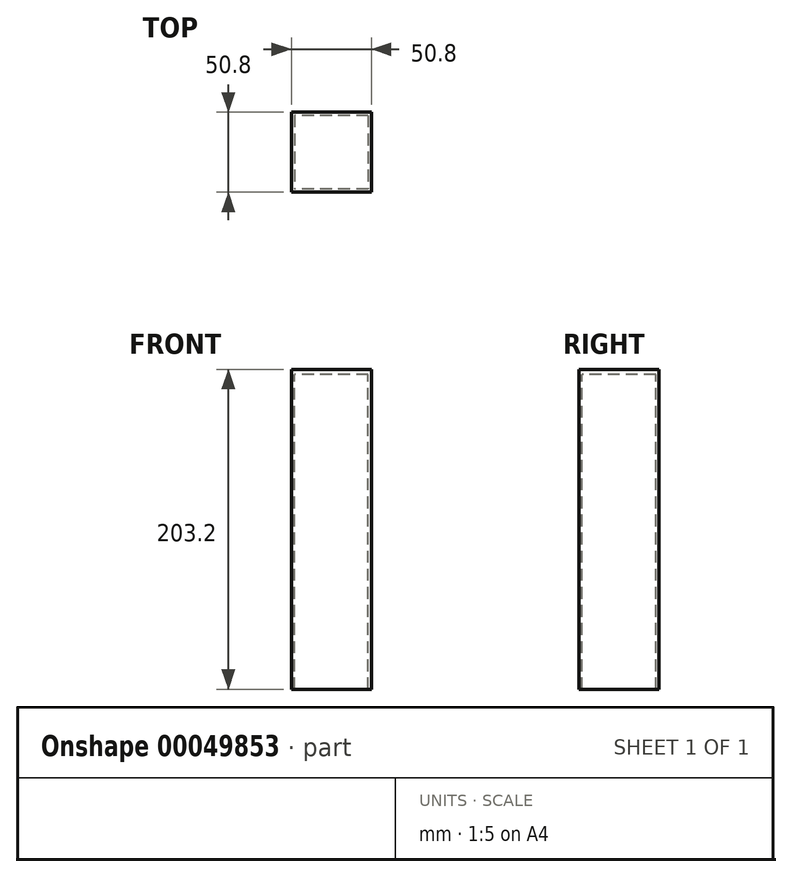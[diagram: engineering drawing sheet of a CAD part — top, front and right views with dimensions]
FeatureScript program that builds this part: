
annotation { "Feature Type Name" : "Feature", "Feature Type Description" : "" }
export const myFeature = defineFeature(function(context is Context, id is Id, definition is map)
    precondition{}
    {
        {
            var Q0;
            Q0=qCreatedBy(makeId("Top.planeOp"),FACE);
            var sketch = newSketch(context, id + "F0", { "sketchPlane" : qUnion([Q0])});
            skLineSegment(sketch, "E0.rect.bottom", {"start": v(25.4, 25.4) * mm, "end": v(-25.4, 25.4) * mm});
            skLineSegment(sketch, "E0.rect.top", {"start": v(25.4, -25.4) * mm, "end": v(-25.4, -25.4) * mm});
            skLineSegment(sketch, "E0.rect.left", {"start": v(25.4, 25.4) * mm, "end": v(25.4, -25.4) * mm});
            skLineSegment(sketch, "E0.rect.right", {"start": v(-25.4, 25.4) * mm, "end": v(-25.4, -25.4) * mm});
            skPoint(sketch, "E0.rect.middle", {"position": v(0, 0) * mm});
            skLineSegment(sketch, "E1.0", {"start": v(23.4, 23.4) * mm, "end": v(-23.4, 23.4) * mm});
            skLineSegment(sketch, "E1.1", {"start": v(23.4, 23.4) * mm, "end": v(23.4, -23.4) * mm});
            skLineSegment(sketch, "E1.2", {"start": v(23.4, -23.4) * mm, "end": v(-23.4, -23.4) * mm});
            skLineSegment(sketch, "E1.3", {"start": v(-23.4, 23.4) * mm, "end": v(-23.4, -23.4) * mm});
            skSolve(sketch);
        }
        {
            var Q0;
            Q0=makeQuery(id+"F0.imprint","IMPRINT",FACE,{"disambiguationData":[TD([[makeQuery(id+"F0.imprint","IMPRINT",EDGE,{"derivedFrom":sQuery(id+"F0.wireOp",EDGE,"E1.0")}),1.0]])]});
            var Q1;
            Q1=makeQuery(id+"F0.imprint","IMPRINT",FACE,{"disambiguationData":[TD([[makeQuery(id+"F0.imprint","IMPRINT",EDGE,{"derivedFrom":sQuery(id+"F0.wireOp",EDGE,"E0.rect.bottom")}),1.0]])]});
            extrude(context, id + "F1", {"entities" : qUnion([Q0, Q1]), "depth" : 3.17 * mm});
        }
        {
            var Q0;
            Q0=makeQuery(id+"F0.imprint","IMPRINT",FACE,{"disambiguationData":[TD([[makeQuery(id+"F0.imprint","IMPRINT",EDGE,{"derivedFrom":sQuery(id+"F0.wireOp",EDGE,"E0.rect.bottom")}),1.0]])]});
            extrude(context, id + "F2", {"entities" : qUnion([Q0]), "operationType" : NewBodyOperationType.ADD, "oppositeDirection" : true, "depth" : 200.02 * mm});
        }
    });
